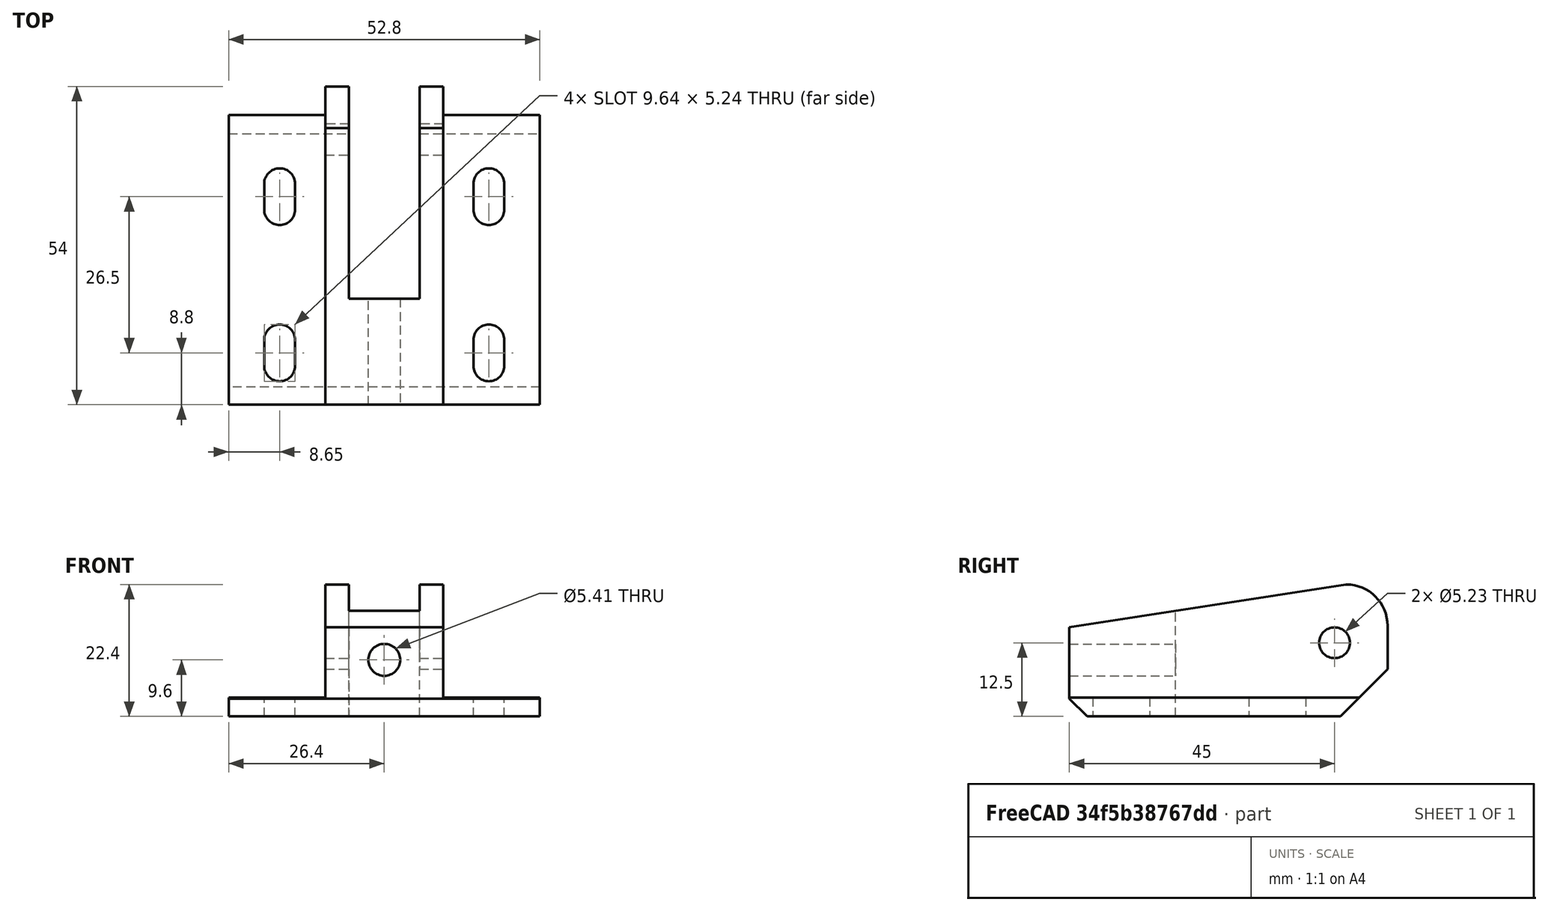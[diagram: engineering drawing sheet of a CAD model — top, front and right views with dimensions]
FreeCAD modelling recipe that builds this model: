
FCSTD DOCUMENT  (FreeCAD 0.21R33668 +26 (Git))
Label: Door Latch catch
License: All rights reserved
LicenseURL: http://en.wikipedia.org/wiki/All_rights_reserved
objects: TechDraw::DrawViewDimension×10, Sketcher::SketchObject×7, PartDesign::Pocket×6, TechDraw::DrawProjGroupItem×4, PartDesign::Chamfer×3, PartDesign::Pad×1, PartDesign::Fillet×1, PartDesign::Body×1, TechDraw::DrawSVGTemplate×1, TechDraw::DrawViewAnnotation×1, TechDraw::DrawProjGroup×1, TechDraw::DrawRichAnno×1, TechDraw::DrawViewImage×1, TechDraw::DrawPage×1
note: 45 computed .brp shape members not serialized (recipe doc carries the construction recipe); baked Part::Feature solids carry a one-line shape summary decoded from their .brp

FEATURE [Sketcher::SketchObject] Sketch
  FullyConstrained = true
  MapMode = 5
  Support = -> [XY_Plane]
  sketch-geometry (4):
    g0: LineSegment StartX=-26.4 StartY=27 StartZ=0 EndX=26.4 EndY=27 EndZ=0
    g1: LineSegment StartX=26.4 StartY=27 StartZ=0 EndX=26.4 EndY=-27 EndZ=0
    g2: LineSegment StartX=26.4 StartY=-27 StartZ=0 EndX=-26.4 EndY=-27 EndZ=0
    g3: LineSegment StartX=-26.4 StartY=-27 StartZ=0 EndX=-26.4 EndY=27 EndZ=0
  constraints (11):
    c: Coincident(g0,g1)
    c: Coincident(g1,g2)
    c: Coincident(g2,g3)
    c: Coincident(g3,g0)
    c: Horizontal(g0)
    c: Horizontal(g2)
    c: Vertical(g1)
    c: Vertical(g3)
    c: Symmetric(g0,g1,g-1)
    c: DistanceX(g0,g0) = 52.8
    c: DistanceY(g1,g0) = 54
FEATURE [PartDesign::Pad] Pad
  Direction = (0,0,1)
  Length = 22.4
  Length2 = 10
  Profile = -> Sketch
  ReferenceAxis = -> Sketch [N_Axis]
  Type = 0
FEATURE [Sketcher::SketchObject] Sketch001
  FullyConstrained = true
  MapMode = 5
  Support = -> [XY_Plane]
  sketch-geometry (8):
    g0: LineSegment StartX=-30 StartY=30 StartZ=0 EndX=-10 EndY=30 EndZ=0
    g1: LineSegment StartX=-10 StartY=30 StartZ=0 EndX=-10 EndY=-30 EndZ=0
    g2: LineSegment StartX=-10 StartY=-30 StartZ=0 EndX=-30 EndY=-30 EndZ=0
    g3: LineSegment StartX=-30 StartY=-30 StartZ=0 EndX=-30 EndY=30 EndZ=0
    g4: LineSegment StartX=10 StartY=30 StartZ=0 EndX=30 EndY=30 EndZ=0
    g5: LineSegment StartX=30 StartY=30 StartZ=0 EndX=30 EndY=-30 EndZ=0
    g6: LineSegment StartX=30 StartY=-30 StartZ=0 EndX=10 EndY=-30 EndZ=0
    g7: LineSegment StartX=10 StartY=-30 StartZ=0 EndX=10 EndY=30 EndZ=0
  constraints (22):
    c: Coincident(g0,g1)
    c: Coincident(g1,g2)
    c: Coincident(g2,g3)
    c: Coincident(g3,g0)
    c: Horizontal(g0)
    c: Horizontal(g2)
    c: Vertical(g3)
    c: Coincident(g4,g5)
    c: Coincident(g5,g6)
    c: Coincident(g6,g7)
    c: Coincident(g7,g4)
    c: Horizontal(g4)
    c: Horizontal(g6)
    c: Vertical(g5)
    c: Vertical(g7)
    c: Equal(g3,g7)
    c: DistanceX(g0,g4) = 20
    c: Symmetric(g0,g4,g-2)
    c: DistanceY(g-1,g0) = 30
    c: Symmetric(g0,g1,g-1)
    c: DistanceX(g0,g0) = 20
    c: Equal(g0,g4)
FEATURE [PartDesign::Pocket] Pocket
  BaseFeature = -> Pad
  Direction = (0,0,-1)
  Length = 23
  Length2 = -3.2
  Profile = -> Sketch001
  ReferenceAxis = -> Sketch001 [N_Axis]
  Reversed = true
  Type = 4
FEATURE [PartDesign::Chamfer] Chamfer001
  Angle = 12
  Base = -> Pocket
  BaseFeature = -> Pocket
  ChamferType = 2
  FlipDirection = false
  Size = 44
  Size2 = 1
  SupportTransform = false
  UseAllEdges = false
FEATURE [Sketcher::SketchObject] Sketch002
  FullyConstrained = true
  MapMode = 5
  Support = -> [XY_Plane]
  sketch-geometry (4):
    g0: LineSegment StartX=-6 StartY=27.5 StartZ=0 EndX=6 EndY=27.5 EndZ=0
    g1: LineSegment StartX=6 StartY=27.5 StartZ=0 EndX=6 EndY=-9 EndZ=0
    g2: LineSegment StartX=6 StartY=-9 StartZ=0 EndX=-6 EndY=-9 EndZ=0
    g3: LineSegment StartX=-6 StartY=-9 StartZ=0 EndX=-6 EndY=27.5 EndZ=0
  constraints (11):
    c: Coincident(g0,g1)
    c: Coincident(g1,g2)
    c: Coincident(g2,g3)
    c: Coincident(g3,g0)
    c: Horizontal(g0)
    c: Vertical(g1)
    c: Vertical(g3)
    c: DistanceY(g2,g0) = 36.5
    c: DistanceX(g2,g1) = 12
    c: Symmetric(g2,g1,g-2)
    c: DistanceY(g1,g-1) = 9
FEATURE [PartDesign::Pocket] Pocket001
  BaseFeature = -> Chamfer001
  Direction = (0,0,-1)
  Length = 23
  Length2 = 5
  Profile = -> Sketch002
  ReferenceAxis = -> Sketch002 [N_Axis]
  Reversed = true
  Type = 0
FEATURE [Sketcher::SketchObject] Sketch003
  FullyConstrained = true
  MapMode = 5
  Placement = pos=(0,0,0) rot=(0.57735,0.57735,0.57735;2.0944rad)
  Support = -> [YZ_Plane]
  sketch-geometry (1):
    g0: Circle CenterX=18 CenterY=12.5 CenterZ=0 NormalX=0 NormalY=0 NormalZ=1 AngleXU=0 Radius=2.615
  constraints (3):
    c: Diameter(g0) = 5.23
    c: DistanceY(g-1,g0) = 12.5
    c: DistanceX(g-1,g0) = 18
FEATURE [PartDesign::Pocket] Pocket002
  BaseFeature = -> Pocket001
  Direction = (-1,2e-16,-3e-16)
  Length = 10
  Length2 = 10
  Profile = -> Sketch003
  ReferenceAxis = -> Sketch003 [N_Axis]
  Type = 4
FEATURE [Sketcher::SketchObject] Sketch004
  FullyConstrained = true
  MapMode = 5
  Support = -> [XY_Plane]
  sketch-geometry (16):
    g0: ArcOfCircle CenterX=-17.75 CenterY=10.5 CenterZ=0 NormalX=0 NormalY=0 NormalZ=1 AngleXU=0 Radius=2.62 StartAngle=0 EndAngle=3.14159
    g1: ArcOfCircle CenterX=-17.75 CenterY=6.1 CenterZ=0 NormalX=0 NormalY=0 NormalZ=1 AngleXU=0 Radius=2.62 StartAngle=3.14159 EndAngle=6.28319
    g2: LineSegment StartX=-20.37 StartY=10.5 StartZ=0 EndX=-20.37 EndY=6.1 EndZ=0
    g3: LineSegment StartX=-15.13 StartY=6.1 StartZ=0 EndX=-15.13 EndY=10.5 EndZ=0
    g4: ArcOfCircle CenterX=-17.75 CenterY=-16 CenterZ=0 NormalX=0 NormalY=0 NormalZ=1 AngleXU=0 Radius=2.62 StartAngle=0 EndAngle=3.14159
    g5: ArcOfCircle CenterX=-17.75 CenterY=-20.4 CenterZ=0 NormalX=0 NormalY=0 NormalZ=1 AngleXU=0 Radius=2.62 StartAngle=3.14159 EndAngle=6.28319
    g6: LineSegment StartX=-20.37 StartY=-16 StartZ=0 EndX=-20.37 EndY=-20.4 EndZ=0
    g7: LineSegment StartX=-15.13 StartY=-20.4 StartZ=0 EndX=-15.13 EndY=-16 EndZ=0
    g8: ArcOfCircle CenterX=17.75 CenterY=-16 CenterZ=0 NormalX=0 NormalY=0 NormalZ=1 AngleXU=0 Radius=2.62 StartAngle=1.77e-14 EndAngle=3.14159
    g9: ArcOfCircle CenterX=17.75 CenterY=-20.4 CenterZ=0 NormalX=0 NormalY=0 NormalZ=1 AngleXU=0 Radius=2.62 StartAngle=3.14159 EndAngle=6.28319
    g10: LineSegment StartX=15.13 StartY=-16 StartZ=0 EndX=15.13 EndY=-20.4 EndZ=0
    g11: LineSegment StartX=20.37 StartY=-20.4 StartZ=0 EndX=20.37 EndY=-16 EndZ=0
    g12: ArcOfCircle CenterX=17.75 CenterY=10.5 CenterZ=0 NormalX=0 NormalY=0 NormalZ=1 AngleXU=0 Radius=2.62 StartAngle=1.8e-14 EndAngle=3.14159
    g13: ArcOfCircle CenterX=17.75 CenterY=6.1 CenterZ=0 NormalX=0 NormalY=0 NormalZ=1 AngleXU=0 Radius=2.62 StartAngle=3.14159 EndAngle=6.28319
    g14: LineSegment StartX=15.13 StartY=10.5 StartZ=0 EndX=15.13 EndY=6.1 EndZ=0
    g15: LineSegment StartX=20.37 StartY=6.1 StartZ=0 EndX=20.37 EndY=10.5 EndZ=0
  constraints (39):
    c: Tangent(g0,g2) = -1.5708
    c: Tangent(g2,g1) = -1.5708
    c: Tangent(g1,g3) = -1.5708
    c: Tangent(g3,g0) = -1.5708
    c: Equal(g0,g1)
    c: Vertical(g2)
    c: Tangent(g4,g6) = -1.5708
    c: Tangent(g6,g5) = -1.5708
    c: Tangent(g5,g7) = -1.5708
    c: Tangent(g7,g4) = -1.5708
    c: Equal(g4,g5)
    c: Vertical(g6)
    c: Tangent(g8,g10) = -1.5708
    c: Tangent(g10,g9) = -1.5708
    c: Tangent(g9,g11) = -1.5708
    c: Tangent(g11,g8) = -1.5708
    c: Equal(g8,g9)
    c: Vertical(g10)
    c: Tangent(g12,g14) = -1.5708
    c: Tangent(g14,g13) = -1.5708
    c: Tangent(g13,g15) = -1.5708
    c: Tangent(g15,g12) = -1.5708
    c: Equal(g12,g13)
    c: Vertical(g14)
    c: Radius(g0) = 2.62
    c: Equal(g0,g12)
    c: Equal(g4,g0)
    c: Equal(g8,g0)
    c: DistanceY(g1,g0) = 4.4
    c: Equal(g2,g14)
    c: Equal(g2,g10)
    c: Equal(g2,g7)
    c: Vertical(g4,g1)
    c: Vertical(g8,g13)
    c: Horizontal(g0,g12)
    c: Symmetric(g4,g8,g-2)
    c: DistanceX(g0,g12) = 35.5
    c: DistanceY(g8,g-1) = 16
    c: DistanceY(g9,g13) = 26.5
FEATURE [PartDesign::Pocket] Pocket003
  BaseFeature = -> Pocket002
  Direction = (0,0,-1)
  Length = 5
  Length2 = 5
  Profile = -> Sketch004
  ReferenceAxis = -> Sketch004 [N_Axis]
  Reversed = true
  Type = 0
FEATURE [Sketcher::SketchObject] Sketch005
  FullyConstrained = true
  MapMode = 5
  Placement = pos=(0,0,0) rot=(1,0,0;1.5708rad)
  Support = -> [XZ_Plane]
  sketch-geometry (1):
    g0: Circle CenterX=0 CenterY=9.6 CenterZ=0 NormalX=0 NormalY=0 NormalZ=1 AngleXU=0 Radius=2.705
  constraints (3):
    c: PointOnObject(g0,g-2)
    c: Diameter(g0) = 5.41
    c: DistanceY(g-1,g0) = 9.6
FEATURE [PartDesign::Pocket] Pocket004
  BaseFeature = -> Pocket003
  Direction = (0,1,2e-16)
  Length = 29
  Length2 = 5
  Profile = -> Sketch005
  ReferenceAxis = -> Sketch005 [N_Axis]
  Reversed = true
  Type = 0
FEATURE [Sketcher::SketchObject] Sketch006
  FullyConstrained = true
  MapMode = 5
  Placement = pos=(0,0,0) rot=(0.57735,0.57735,0.57735;2.0944rad)
  Support = -> [YZ_Plane]
  sketch-geometry (3):
    g0: LineSegment StartX=-28 StartY=25 StartZ=0 EndX=36.75 EndY=25 EndZ=0
    g1: LineSegment StartX=36.75 StartY=25 StartZ=0 EndX=-28 EndY=15 EndZ=0
    g2: LineSegment StartX=-28 StartY=15 StartZ=0 EndX=-28 EndY=25 EndZ=0
  constraints (9):
    c: Horizontal(g0)
    c: Coincident(g1,g0)
    c: Coincident(g2,g1)
    c: Coincident(g2,g0)
    c: Vertical(g2)
    c: DistanceY(g1,g0) = 10
    c: DistanceY(g-1,g0) = 25
    c: DistanceX(g0,g0) = 64.75
    c: DistanceX(g0,g-1) = 28
FEATURE [PartDesign::Pocket] Pocket005
  BaseFeature = -> Pocket004
  Direction = (-1,2e-16,-3e-16)
  Length = 10
  Length2 = 10
  Profile = -> Sketch006
  ReferenceAxis = -> Sketch006 [N_Axis]
  Type = 4
FEATURE [PartDesign::Fillet] Fillet
  Base = -> Pocket005 [Edge3,Edge67]
  BaseFeature = -> Pocket005
  Radius = 7
  SupportTransform = false
  UseAllEdges = false
FEATURE [PartDesign::Chamfer] Chamfer
  Angle = 45
  Base = -> Fillet [Edge3,Edge20]
  BaseFeature = -> Fillet
  ChamferType = 0
  FlipDirection = false
  Size = 8
  Size2 = 1
  SupportTransform = false
  UseAllEdges = false
FEATURE [PartDesign::Chamfer] Chamfer002
  Angle = 45
  Base = -> Chamfer [Edge24]
  BaseFeature = -> Chamfer
  ChamferType = 0
  FlipDirection = false
  Size = 3
  Size2 = 1
  SupportTransform = false
  UseAllEdges = false
FEATURE [PartDesign::Body] Body
  Group = -> [Sketch,Pad,Sketch001,Pocket,Chamfer001,Sketch002,Pocket001,Sketch003,Pocket002,Sketch004,Pocket003,Sketch005,Pocket004,Sketch006,Pocket005,Fillet,Chamfer,Chamfer002]
  Origin = -> Origin
  Tip = -> Chamfer002
FEATURE [TechDraw::DrawSVGTemplate] Template
  EditableTexts = Designed_by_Name=Chris Howell; Drawing_number=2024091601; FC-Date=16 September 2024; FC-SH=1; FC-Title=Door Latch Catch
  Height = 210
  Orientation = 1
  Template = C:/Program Files/FreeCAD 0.21/data/Mod/TechDraw/Templates/A4_LandscapeTD.svg
  Width = 297
FEATURE [TechDraw::DrawProjGroupItem] ProjItem  label="Front"
  CoarseView = true
  Direction = (0,0,1)
  Focus = 100
  HardHidden = true
  IsoCount = 0
  IsoHidden = false
  IsoVisible = false
  LockPosition = true
  Perspective = false
  Rotation = 0
  RotationVector = (1,0,0)
  ScaleType = 2
  ScrubCount = 0
  SeamHidden = false
  SeamVisible = false
  SmoothHidden = false
  SmoothVisible = true
  Source = -> [Body]
  Type = 0
  X = 0
  XDirection = (1,0,0)
  Y = 0
FEATURE [TechDraw::DrawProjGroupItem] ProjItem006  label="Left"
  CoarseView = false
  Direction = (-1,0,1e-16)
  Focus = 100
  HardHidden = true
  IsoCount = 0
  IsoHidden = false
  IsoVisible = false
  LockPosition = false
  Perspective = false
  Rotation = 0
  RotationVector = (1,0,0)
  ScaleType = 2
  ScrubCount = 0
  SeamHidden = false
  SeamVisible = false
  SmoothHidden = false
  SmoothVisible = false
  Source = -> [Body]
  Type = 1
  X = -67.6
  XDirection = (1e-16,0,1)
  Y = 0
FEATURE [TechDraw::DrawProjGroupItem] ProjItem007  label="Bottom"
  CoarseView = false
  Direction = (0,-1,0)
  Focus = 100
  HardHidden = false
  IsoCount = 0
  IsoHidden = false
  IsoVisible = false
  LockPosition = false
  Perspective = false
  Rotation = 0
  RotationVector = (1,0,0)
  ScaleType = 2
  ScrubCount = 0
  SeamHidden = false
  SeamVisible = false
  SmoothHidden = false
  SmoothVisible = true
  Source = -> [Body]
  Type = 5
  X = 0
  XDirection = (1,0,0)
  Y = -68.2
FEATURE [TechDraw::DrawViewDimension] Dimension
  AngleOverride = false
  Arbitrary = false
  ArbitraryTolerances = false
  EqualTolerance = true
  ExtensionAngle = 0
  FormatSpec = %.2w
  FormatSpecOverTolerance = %+.2w
  FormatSpecUnderTolerance = %+.2w
  Inverted = false
  LineAngle = 0
  LockPosition = false
  MeasureType = 1
  OverTolerance = 0
  References2D = -> [ProjItem]
  Rotation = 0
  ScaleType = 0
  TheoreticalExact = false
  Type = 1
  UnderTolerance = 0
  X = -1.9656
  Y = 49.728
FEATURE [TechDraw::DrawViewDimension] Dimension001
  AngleOverride = false
  Arbitrary = false
  ArbitraryTolerances = false
  EqualTolerance = true
  ExtensionAngle = 0
  FormatSpec = %.2w
  FormatSpecOverTolerance = %+.2w
  FormatSpecUnderTolerance = %+.2w
  Inverted = false
  LineAngle = 0
  LockPosition = false
  MeasureType = 1
  OverTolerance = 0
  References2D = -> [ProjItem]
  Rotation = 0
  ScaleType = 0
  TheoreticalExact = false
  Type = 2
  UnderTolerance = 0
  X = 46.7045
  Y = 1.09907
FEATURE [TechDraw::DrawViewDimension] Dimension002
  AngleOverride = false
  Arbitrary = false
  ArbitraryTolerances = false
  EqualTolerance = true
  ExtensionAngle = 0
  FormatSpec = %.2w
  FormatSpecOverTolerance = %+.2w
  FormatSpecUnderTolerance = %+.2w
  Inverted = false
  LineAngle = 0
  LockPosition = false
  MeasureType = 1
  OverTolerance = 0
  References2D = -> [ProjItem]
  Rotation = 0
  ScaleType = 0
  TheoreticalExact = false
  Type = 1
  UnderTolerance = 0
  X = 37.5032
  Y = -34.0107
FEATURE [TechDraw::DrawViewDimension] Dimension003
  AngleOverride = false
  Arbitrary = false
  ArbitraryTolerances = false
  EqualTolerance = true
  ExtensionAngle = 0
  FormatSpec = %.2w
  FormatSpecOverTolerance = %+.2w
  FormatSpecUnderTolerance = %+.2w
  Inverted = false
  LineAngle = 0
  LockPosition = false
  MeasureType = 1
  OverTolerance = 0
  References2D = -> [ProjItem]
  Rotation = 0
  ScaleType = 0
  TheoreticalExact = false
  Type = 2
  UnderTolerance = 0
  X = -43.3453
  Y = 1.8514
FEATURE [TechDraw::DrawViewDimension] Dimension004
  AngleOverride = false
  Arbitrary = false
  ArbitraryTolerances = false
  EqualTolerance = true
  ExtensionAngle = 0
  FormatSpec = %.2w
  FormatSpecOverTolerance = %+.2w
  FormatSpecUnderTolerance = %+.2w
  Inverted = false
  LineAngle = 0
  LockPosition = false
  MeasureType = 1
  OverTolerance = 0
  References2D = -> [ProjItem007]
  Rotation = 0
  ScaleType = 0
  TheoreticalExact = false
  Type = 2
  UnderTolerance = 0
  X = 40.6149
  Y = -1.28252
FEATURE [TechDraw::DrawViewAnnotation] Annotation
  Font = osifont
  LineSpace = 100
  LockPosition = false
  MaxWidth = -1
  Rotation = 0
  ScaleType = 0
  Text = Tap 0.250" 1/4 - 28 Thread
  TextSize = 5
  TextStyle = 0
  X = 235.832
  Y = 96.9692
FEATURE [TechDraw::DrawViewDimension] Dimension007
  AngleOverride = false
  Arbitrary = false
  ArbitraryTolerances = false
  EqualTolerance = true
  ExtensionAngle = 0
  FormatSpec = %.2w
  FormatSpecOverTolerance = %+.2w
  FormatSpecUnderTolerance = %+.2w
  Inverted = false
  LineAngle = 0
  LockPosition = false
  MeasureType = 1
  OverTolerance = 0
  References2D = -> [ProjItem]
  Rotation = 0
  ScaleType = 0
  TheoreticalExact = false
  Type = 1
  UnderTolerance = 0
  X = -18.2218
  Y = 37.3336
FEATURE [TechDraw::DrawViewDimension] Dimension008
  AngleOverride = false
  Arbitrary = false
  ArbitraryTolerances = false
  EqualTolerance = true
  ExtensionAngle = 0
  FormatSpec = %.2w
  FormatSpecOverTolerance = %+.2w
  FormatSpecUnderTolerance = %+.2w
  Inverted = false
  LineAngle = 0
  LockPosition = false
  MeasureType = 1
  OverTolerance = 0
  References2D = -> [ProjItem]
  Rotation = 0
  ScaleType = 0
  TheoreticalExact = false
  Type = 1
  UnderTolerance = 0
  X = 15.4875
  Y = 41.9849
FEATURE [TechDraw::DrawViewDimension] Dimension009
  AngleOverride = false
  Arbitrary = false
  ArbitraryTolerances = false
  EqualTolerance = true
  ExtensionAngle = 0
  FormatSpec = %.2w
  FormatSpecOverTolerance = %+.2w
  FormatSpecUnderTolerance = %+.2w
  Inverted = false
  LineAngle = 0
  LockPosition = false
  MeasureType = 1
  OverTolerance = 0
  References2D = -> [ProjItem006]
  Rotation = 0
  ScaleType = 0
  TheoreticalExact = false
  Type = 2
  UnderTolerance = 0
  X = -25.101
  Y = -16.0621
FEATURE [TechDraw::DrawViewDimension] Dimension010
  AngleOverride = false
  Arbitrary = false
  ArbitraryTolerances = false
  EqualTolerance = true
  ExtensionAngle = 0
  FormatSpec = ⌀%.2w
  FormatSpecOverTolerance = %+.2w
  FormatSpecUnderTolerance = %+.2w
  Inverted = false
  LineAngle = 0
  LockPosition = false
  MeasureType = 1
  OverTolerance = 0
  References2D = -> [ProjItem007]
  Rotation = 0
  ScaleType = 0
  TheoreticalExact = false
  Type = 5
  UnderTolerance = 0
  X = 74.9884
  Y = 8.97757
FEATURE [TechDraw::DrawViewDimension] Dimension011
  AngleOverride = false
  Arbitrary = false
  ArbitraryTolerances = false
  EqualTolerance = true
  ExtensionAngle = 0
  FormatSpec = %.2w
  FormatSpecOverTolerance = %+.2w
  FormatSpecUnderTolerance = %+.2w
  Inverted = false
  LineAngle = 0
  LockPosition = false
  MeasureType = 1
  OverTolerance = 0
  References2D = -> [ProjItem007]
  Rotation = 0
  ScaleType = 0
  TheoreticalExact = false
  Type = 2
  UnderTolerance = 0
  X = 28.0862
  Y = 4.32209
FEATURE [TechDraw::DrawProjGroupItem] ProjItem008  label="Right"
  CoarseView = false
  Direction = (1,0,1e-16)
  Focus = 100
  HardHidden = false
  IsoCount = 0
  IsoHidden = false
  IsoVisible = false
  LockPosition = false
  Perspective = false
  Rotation = 0
  RotationVector = (1,0,0)
  ScaleType = 2
  ScrubCount = 0
  SeamHidden = false
  SeamVisible = false
  SmoothHidden = false
  SmoothVisible = true
  Source = -> [Body]
  Type = 2
  X = 67.6
  XDirection = (1e-16,0,-1)
  Y = 0
FEATURE [TechDraw::DrawProjGroup] ProjGroup
  Anchor = -> ProjItem
  AutoDistribute = true
  LockPosition = false
  ProjectionType = 1
  Rotation = 0
  ScaleType = 0
  Source = -> [Body]
  Views = -> [ProjItem,ProjItem006,ProjItem007,ProjItem008]
  X = 147.394
  Y = 149.773
  spacingX = 30
  spacingY = 30
FEATURE [TechDraw::DrawRichAnno] RichTextAnnotation
  AnnoText = <!DOCTYPE HTML PUBLIC "-//W3C//DTD HTML 4.0//EN" "http://www.w3.org/TR/REC-html40/strict.dtd">\n<html><head><meta name="qrichtext" content="1" /><style type="text/css">\np, li { white-space: pre-wrap; }\n</style></head><body style=" font-family:'MS Shell Dlg 2'; font-size:7.8pt; font-weight:400; font-style:normal;">\n<p style="-qt-paragraph-type:empty; margin-top:0px; margin-bottom:0px; margin-left:0px; margin-right:0px; -qt-block-indent:0; text-indent:0px;"><br /></p></body></html>
  LockPosition = false
  MaxWidth = -1
  Rotation = 0
  ScaleType = 0
  ShowFrame = false
  X = 148.5
  Y = 105
FEATURE [TechDraw::DrawViewImage] ActiveView  label="3D View"
  Height = 200
  ImageFile = <userpath>/AppData/Local/Temp/FreeCAD/Cache/FreeCAD_Doc_ddc9dec3-aeef-40ce-b5af-f1efee88cc0e_eac1cb_19604/PagEEF5.tmp.png
  LockPosition = false
  Rotation = 0
  Scale = 1.6
  ScaleType = 2
  Width = 200
  X = 69.7766
  Y = 73.1458
FEATURE [TechDraw::DrawPage] Page
  KeepUpdated = true
  NextBalloonIndex = 1
  ProjectionType = 0
  Template = -> Template
  Views = -> [ProjGroup,Dimension,Dimension001,Dimension002,Dimension003,Dimension004,Annotation,Dimension007,Dimension008,Dimension009,Dimension010,Dimension011,RichTextAnnotation,ActiveView]
